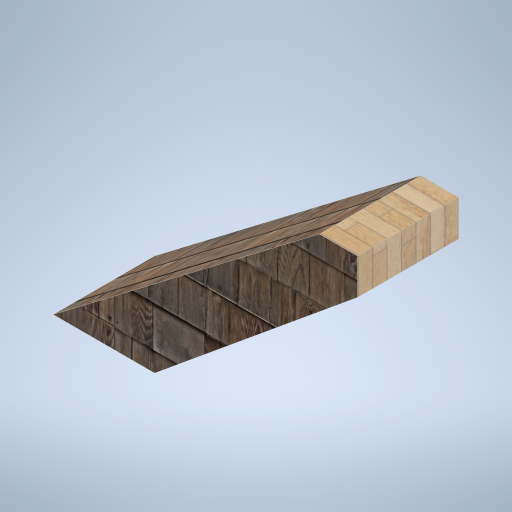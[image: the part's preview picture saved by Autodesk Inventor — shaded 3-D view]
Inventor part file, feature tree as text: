
AUTODESK INVENTOR PART (.ipt)
format: ipt  version: 2024.2 (Build 282272000, 272)  size: 329,216 bytes
history: native  units: in
note: dims shown in document units (in); Inventor stores cm internally (conversion verified against a paired STEP export)
features: other x3, sketch x1
ambient origin geometry x8: Origin, YZ Plane, XZ Plane, XY Plane, X Axis, Y Axis, Z Axis, Center Point
bodies: Body1 (feature_tree)
feature tree (4):
  other  "frame_rib_02_MIR.ipt"
  other  "Solid3::frame_rib_02_MIR.ipt"
  other  "TaggingFeature1"
  sketch  "Sketch1"  dims[d0=0.3937in]
